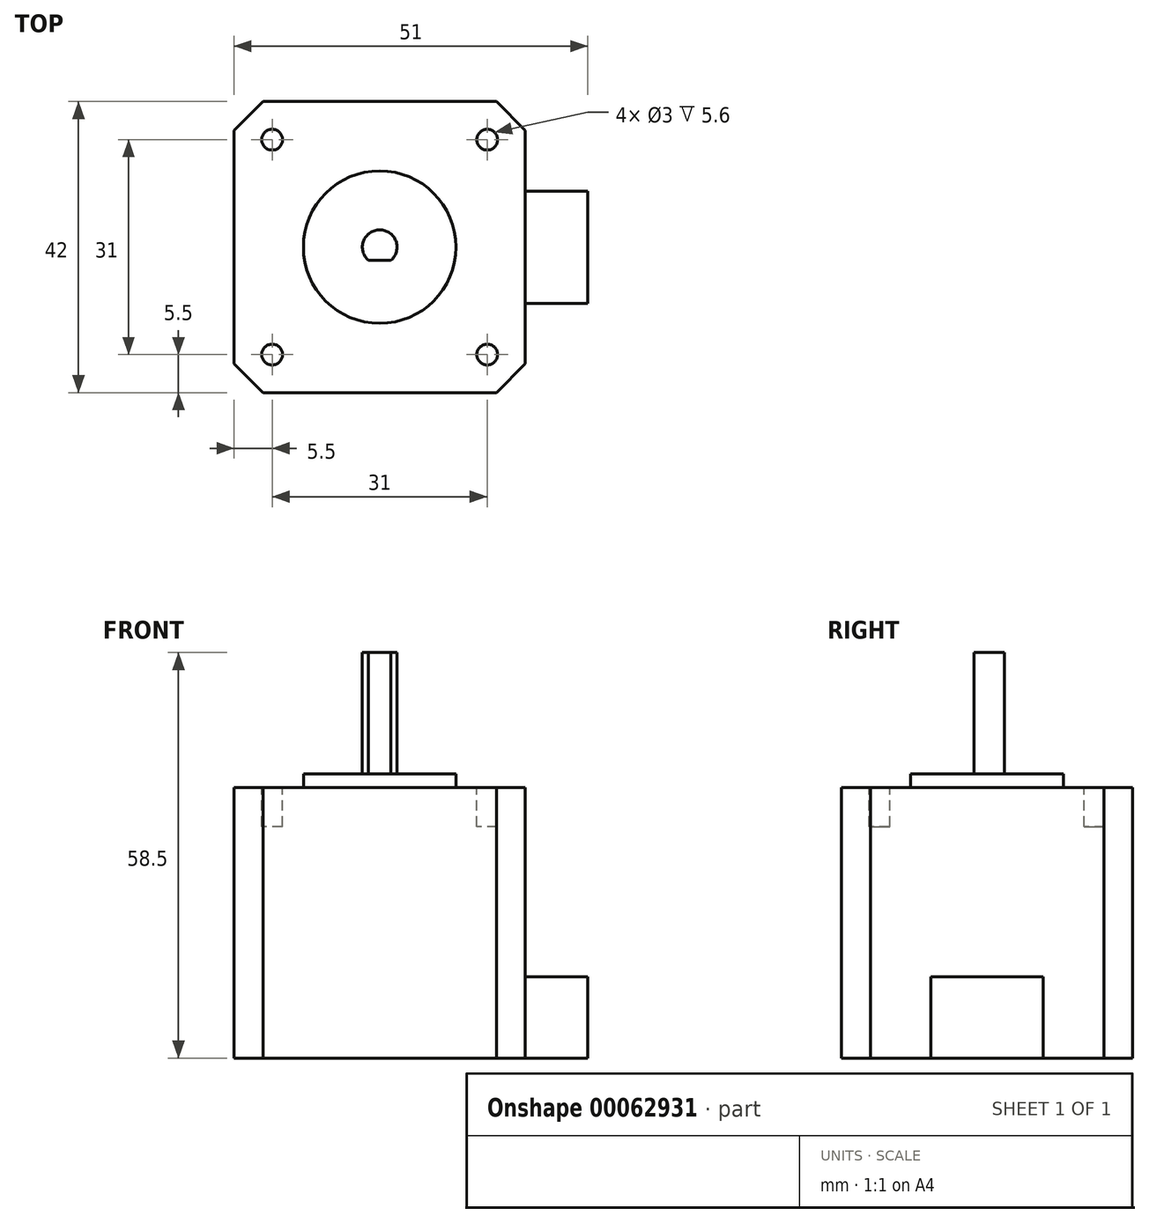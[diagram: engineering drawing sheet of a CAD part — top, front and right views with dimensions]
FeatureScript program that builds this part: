
annotation { "Feature Type Name" : "Feature", "Feature Type Description" : "" }
export const myFeature = defineFeature(function(context is Context, id is Id, definition is map)
    precondition{}
    {
        {
            var Q0;
            Q0=qCreatedBy(makeId("Top.planeOp"),FACE);
            var sketch = newSketch(context, id + "F0", { "sketchPlane" : qUnion([Q0])});
            skLineSegment(sketch, "E0.bottom", {"start": v(0, 0) * mm, "end": v(33.66, 0) * mm});
            skLineSegment(sketch, "E0.top", {"start": v(0, 42) * mm, "end": v(33.66, 42) * mm});
            skLineSegment(sketch, "E0.left", {"start": v(-4.17, 4.17) * mm, "end": v(-4.17, 37.83) * mm});
            skLineSegment(sketch, "E0.right", {"start": v(37.83, 4.17) * mm, "end": v(37.83, 37.83) * mm});
            skLineSegment(sketch, "E1", {"start": v(0, 42) * mm, "end": v(-4.17, 37.83) * mm});
            skLineSegment(sketch, "E2", {"start": v(-4.17, 4.17) * mm, "end": v(0, 0) * mm});
            skLineSegment(sketch, "E3", {"start": v(33.66, 0) * mm, "end": v(37.83, 4.17) * mm});
            skLineSegment(sketch, "E4", {"start": v(37.83, 37.83) * mm, "end": v(33.66, 42) * mm});
            skSolve(sketch);
        }
        {
            var Q0;
            Q0 = qSketchRegion(id + "F0", true);
            extrude(context, id + "F1", {"entities" : qUnion([Q0]), "depth" : 39 * mm});
        }
        {
            var Q0;
            Q0=makeQuery(id+"F1.opExtrude","CAP_FACE",FACE,{"disambiguationData":[OSD([sQuery(id+"F0.wireOp",EDGE,"E0.bottom"),sQuery(id+"F0.wireOp",EDGE,"E0.top"),sQuery(id+"F0.wireOp",EDGE,"E0.left"),sQuery(id+"F0.wireOp",EDGE,"E0.right"),sQuery(id+"F0.wireOp",EDGE,"E1"),sQuery(id+"F0.wireOp",EDGE,"E2"),sQuery(id+"F0.wireOp",EDGE,"E3"),sQuery(id+"F0.wireOp",EDGE,"E4")])],"isStart":false});
            var sketch = newSketch(context, id + "F2", { "sketchPlane" : qUnion([Q0])});
            skCircle(sketch, "E5", {"center": v(16.83, 21) * mm, "radius": 11 * mm});
            skSolve(sketch);
        }
        {
            var Q0;
            Q0 = qSketchRegion(id + "F2", true);
            extrude(context, id + "F3", {"entities" : qUnion([Q0]), "operationType" : NewBodyOperationType.ADD, "depth" : 2 * mm});
        }
        {
            var Q0;
            Q0=makeQuery(id+"F3.opExtrude","CAP_FACE",FACE,{"disambiguationData":[OSD([sQuery(id+"F2.wireOp",EDGE,"E5")])],"isStart":false});
            var sketch = newSketch(context, id + "F4", { "sketchPlane" : qUnion([Q0])});
            skArc(sketch, "E6", {"start": v(18.46, 19.1) * mm, "mid": v(16.83, 23.5) * mm, "end": v(15.2, 19.1) * mm});
            skLineSegment(sketch, "E7", {"start": v(15.2, 19.1) * mm, "end": v(18.46, 19.1) * mm});
            skSolve(sketch);
        }
        {
            var Q0;
            Q0 = qSketchRegion(id + "F4", true);
            extrude(context, id + "F5", {"entities" : qUnion([Q0]), "operationType" : NewBodyOperationType.ADD, "depth" : 17.5 * mm});
        }
        {
            var Q0;
            Q0=makeQuery(id+"F1.opExtrude","SWEPT_FACE",FACE,{"disambiguationData":[OSD([sQuery(id+"F0.wireOp",EDGE,"E0.right")])]});
            var sketch = newSketch(context, id + "F6", { "sketchPlane" : qUnion([Q0])});
            skLineSegment(sketch, "E8.bottom", {"start": v(29.1, 11.7) * mm, "end": v(12.9, 11.7) * mm});
            skLineSegment(sketch, "E8.top", {"start": v(29.1, 0) * mm, "end": v(12.9, 0) * mm});
            skLineSegment(sketch, "E8.left", {"start": v(29.1, 11.7) * mm, "end": v(29.1, 0) * mm});
            skLineSegment(sketch, "E8.right", {"start": v(12.9, 11.7) * mm, "end": v(12.9, 0) * mm});
            skLineSegment(sketch, "E9", {"start": v(21, 39) * mm, "end": v(21, 0) * mm, "construction": true});
            skSolve(sketch);
        }
        {
            var Q0;
            Q0 = qSketchRegion(id + "F6", true);
            extrude(context, id + "F7", {"entities" : qUnion([Q0]), "operationType" : NewBodyOperationType.ADD, "depth" : 9 * mm});
        }
        {
            var Q0;
            Q0=makeQuery(id+"F1.opExtrude","CAP_FACE",FACE,{"disambiguationData":[OSD([sQuery(id+"F0.wireOp",EDGE,"E0.bottom"),sQuery(id+"F0.wireOp",EDGE,"E0.top"),sQuery(id+"F0.wireOp",EDGE,"E0.left"),sQuery(id+"F0.wireOp",EDGE,"E0.right"),sQuery(id+"F0.wireOp",EDGE,"E1"),sQuery(id+"F0.wireOp",EDGE,"E2"),sQuery(id+"F0.wireOp",EDGE,"E3"),sQuery(id+"F0.wireOp",EDGE,"E4")])],"isStart":false});
            var sketch = newSketch(context, id + "F8", { "sketchPlane" : qUnion([Q0])});
            skCircle(sketch, "E10", {"center": v(1.33, 36.5) * mm, "radius": 1.5 * mm});
            skCircle(sketch, "E11", {"center": v(32.33, 36.5) * mm, "radius": 1.5 * mm});
            skCircle(sketch, "E12", {"center": v(32.33, 5.5) * mm, "radius": 1.5 * mm});
            skCircle(sketch, "E13", {"center": v(1.33, 5.5) * mm, "radius": 1.5 * mm});
            skLineSegment(sketch, "E14", {"start": v(1.33, 36.5) * mm, "end": v(32.33, 5.5) * mm, "construction": true});
            skLineSegment(sketch, "E15", {"start": v(32.33, 36.5) * mm, "end": v(1.33, 5.5) * mm, "construction": true});
            skPoint(sketch, "E16", {"position": v(16.83, 21) * mm});
            skSolve(sketch);
        }
        {
            var Q0;
            Q0 = qSketchRegion(id + "F8", true);
            extrude(context, id + "F9", {"entities" : qUnion([Q0]), "operationType" : NewBodyOperationType.REMOVE, "oppositeDirection" : true, "depth" : 5.6 * mm});
        }
    });
